# Revit family: 11 OVERTIME Evo Mesh
name_source: partatom
category: Arredi
units: mm (PartAtom-declared; Revit-internal decimal feet)

## family parameters
Basato su piano di lavoro = Sì
Condiviso = No
Punto di calcolo locali = No
Sempre verticale = Sì
Taglio con vuoti quando caricato = No

## types (16) — shared parameters
Bracciolo 1D = No
Imbottiture = 3518_Luxy_Imbottiture
Prospetto di default = 1219 mm
Struttura = 3518_Luxy_Struttura

## per-type parameters (varying)
| type | Bracciolo 3D | Gambe Fisse | Mec_Syncron | Poggiatesta | Ruote 50 | Ruote 65 | Soluzione |
| 5700_4OMDI18 | Sì | No | Sì | Sì | No | Sì | 3 |
| 5700_4OMDI24 | Sì | No | Sì | Sì | Sì | No | 2 |
| 5710R_4OMGI50 | Sì | No | Sì | No | No | Sì | 3 |
| 5710R_4OMGI56 | Sì | No | Sì | No | Sì | No | 2 |
| 5710_4OMGI58 | No | No | Sì | No | No | Sì | 3 |
| 5710_4OMGI64 | No | No | Sì | No | Sì | No | 2 |
| 5800_4OMDI26 | Sì | No | Sì | Sì | No | Sì | 3 |
| 5800_4OMDI32 | Sì | No | Sì | Sì | Sì | No | 2 |
| 5810R_4OMGI66 | Sì | No | Sì | No | No | Sì | 3 |
| 5810R_4OMGI72 | Sì | No | Sì | No | Sì | No | 2 |
| 5810_4OMGI74 | No | No | Sì | No | No | Sì | 3 |
| 5810_4OMGI80 | No | No | Sì | No | Sì | No | 2 |
| 5600R_4OMFI02 | Sì | Sì | No | No | No | No | 1 |
| 5600R_4OMFI08 | Sì | Sì | No | No | No | No | 1 |
| 5600_4OMFI10 | No | Sì | No | No | No | No | 1 |
| 5600_4OMFI16 | No | Sì | No | No | No | No | 1 |

## geometry (parser evidence)
native form markers: Sweep x2
no freeform markers — native parametric forms only
